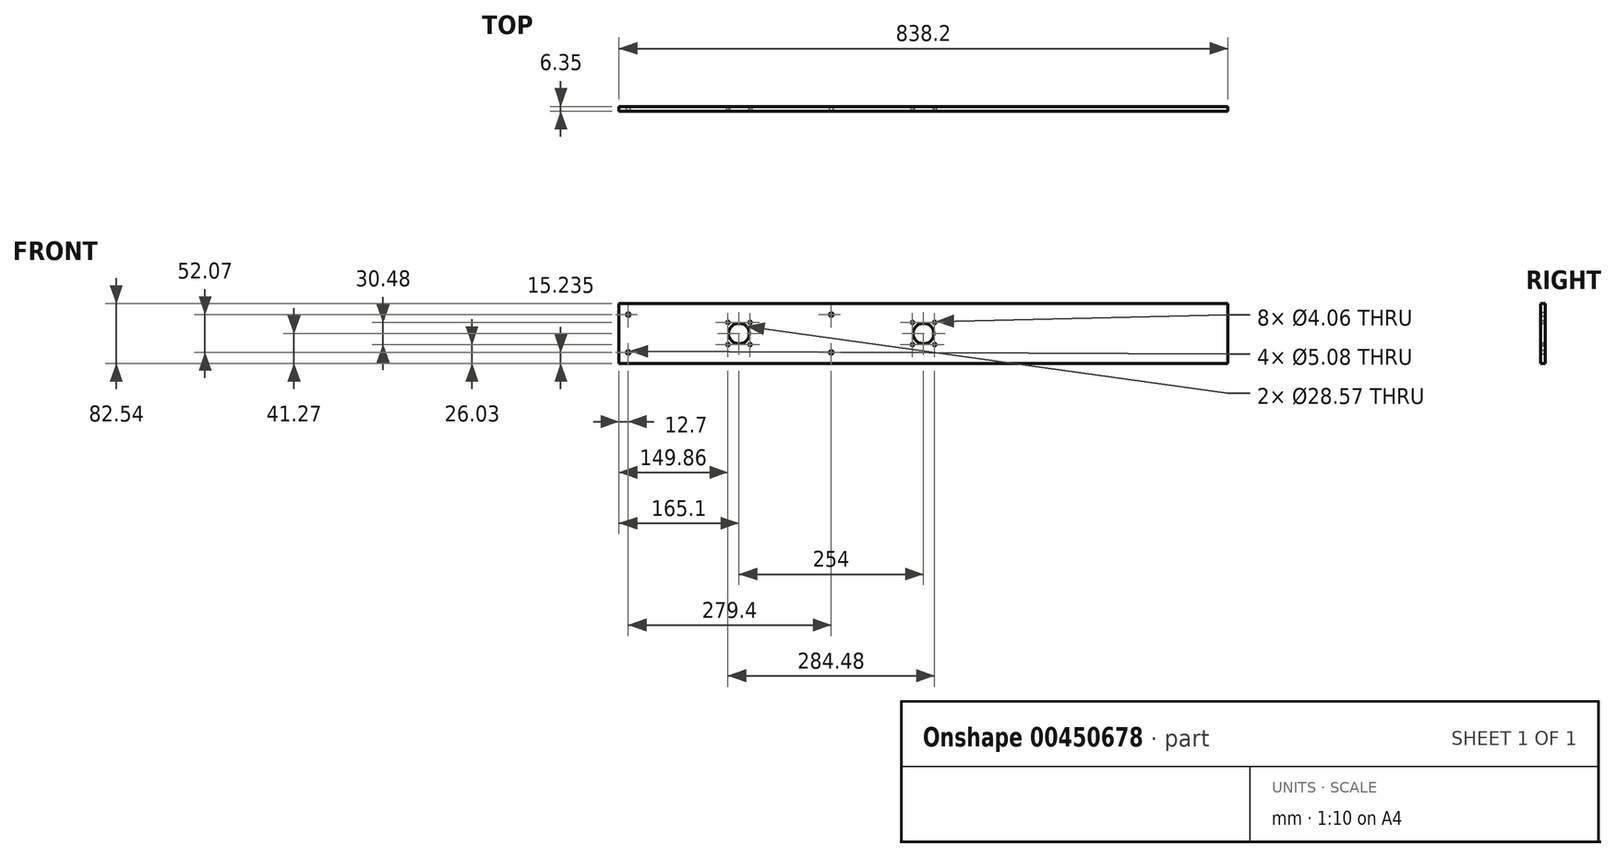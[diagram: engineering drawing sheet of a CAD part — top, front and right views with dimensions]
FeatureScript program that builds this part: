
annotation { "Feature Type Name" : "Feature", "Feature Type Description" : "" }
export const myFeature = defineFeature(function(context is Context, id is Id, definition is map)
    precondition{}
    {
        {
            var Q0;
            Q0=qCreatedBy(makeId("Front.planeOp"),FACE);
            var sketch = newSketch(context, id + "F0", { "sketchPlane" : qUnion([Q0])});
            skLineSegment(sketch, "E0.bottom", {"start": v(419.1, 41.28) * mm, "end": v(-419.1, 41.28) * mm});
            skLineSegment(sketch, "E0.top", {"start": v(419.1, -41.28) * mm, "end": v(-419.1, -41.28) * mm});
            skLineSegment(sketch, "E0.left", {"start": v(419.1, 41.28) * mm, "end": v(419.1, -41.28) * mm});
            skLineSegment(sketch, "E0.right", {"start": v(-419.1, 41.28) * mm, "end": v(-419.1, -41.28) * mm});
            skPoint(sketch, "E0.middle", {"position": v(0, 0) * mm});
            skSolve(sketch);
        }
        {
            var Q0;
            Q0=makeQuery(id+"F0.imprint","IMPRINT",FACE,{"disambiguationData":[TD([[makeQuery(id+"F0.imprint","IMPRINT",EDGE,{"derivedFrom":sQuery(id+"F0.wireOp",EDGE,"E0.bottom")}),1.0]])]});
            extrude(context, id + "F1", {"entities" : qUnion([Q0]), "depth" : 6.35 * mm});
        }
        {
            var Q0;
            Q0=makeQuery(id+"F1.opExtrude","CAP_FACE",FACE,{"disambiguationData":[OSD([sQuery(id+"F0.wireOp",EDGE,"E0.bottom"),sQuery(id+"F0.wireOp",EDGE,"E0.top"),sQuery(id+"F0.wireOp",EDGE,"E0.left"),sQuery(id+"F0.wireOp",EDGE,"E0.right")])],"isStart":false});
            var sketch = newSketch(context, id + "F2", { "sketchPlane" : qUnion([Q0])});
            skLineSegment(sketch, "E1", {"start": v(-419.1, 0) * mm, "end": v(-254, 0) * mm});
            skLineSegment(sketch, "E2", {"start": v(-254, 0) * mm, "end": v(-254, 15.24) * mm});
            skLineSegment(sketch, "E3", {"start": v(-254, 15.24) * mm, "end": v(-269.24, 15.24) * mm});
            skLineSegment(sketch, "E4", {"start": v(-269.24, 15.24) * mm, "end": v(-269.24, -15.24) * mm});
            skLineSegment(sketch, "E5", {"start": v(-269.24, -15.24) * mm, "end": v(-238.76, -15.24) * mm});
            skLineSegment(sketch, "E6", {"start": v(-238.76, -15.24) * mm, "end": v(-238.76, 15.24) * mm});
            skCircle(sketch, "E7", {"center": v(-269.24, 15.24) * mm, "radius": 2.03 * mm});
            skCircle(sketch, "E8", {"center": v(-269.24, -15.24) * mm, "radius": 2.03 * mm});
            skCircle(sketch, "E9", {"center": v(-238.76, -15.24) * mm, "radius": 2.03 * mm});
            skCircle(sketch, "E10", {"center": v(-238.76, 15.24) * mm, "radius": 2.03 * mm});
            skCircle(sketch, "E11", {"center": v(-254, 0) * mm, "radius": 14.29 * mm});
            skLineSegment(sketch, "E12", {"start": v(0, 0) * mm, "end": v(0, 15.24) * mm});
            skLineSegment(sketch, "E13", {"start": v(0, 15.24) * mm, "end": v(-15.24, 15.24) * mm});
            skLineSegment(sketch, "E14", {"start": v(-15.24, 15.24) * mm, "end": v(-15.24, -15.24) * mm});
            skLineSegment(sketch, "E15", {"start": v(-15.24, -15.24) * mm, "end": v(15.24, -15.24) * mm});
            skLineSegment(sketch, "E16", {"start": v(15.24, -15.24) * mm, "end": v(15.24, 15.24) * mm});
            skCircle(sketch, "E17", {"center": v(-15.24, 15.24) * mm, "radius": 2.03 * mm});
            skCircle(sketch, "E18", {"center": v(-15.24, -15.24) * mm, "radius": 2.03 * mm});
            skCircle(sketch, "E19", {"center": v(15.24, -15.24) * mm, "radius": 2.03 * mm});
            skCircle(sketch, "E20", {"center": v(15.24, 15.24) * mm, "radius": 2.03 * mm});
            skCircle(sketch, "E21", {"center": v(0, 0) * mm, "radius": 14.29 * mm});
            skSolve(sketch);
        }
        {
            var Q0;
            {var subQ0=sQuery(id+"F2.wireOp",EDGE,"E4");var subQ1=sQuery(id+"F2.wireOp",EDGE,"E3");var subQ2=makeQuery(id+"F2.imprint","INTERSECT",VERTEX,{"derivedFrom":[subQ1,subQ0]});Q0=makeQuery(id+"F2.imprint","IMPRINT",FACE,{"disambiguationData":[TD([[makeQuery(id+"F2.imprint","IMPRINT",EDGE,{"disambiguationData":[TD([[subQ2,1.0]])],"derivedFrom":subQ1}),-1.0]])]});}
            var Q1;
            {var subQ0=sQuery(id+"F2.wireOp",EDGE,"E4");var subQ1=sQuery(id+"F2.wireOp",EDGE,"E3");var subQ2=makeQuery(id+"F2.imprint","INTERSECT",VERTEX,{"derivedFrom":[subQ1,subQ0]});Q1=makeQuery(id+"F2.imprint","IMPRINT",FACE,{"disambiguationData":[TD([[makeQuery(id+"F2.imprint","IMPRINT",EDGE,{"disambiguationData":[TD([[subQ2,1.0]])],"derivedFrom":subQ1}),1.0]])]});}
            var Q2;
            {var subQ0=sQuery(id+"F2.wireOp",EDGE,"E2");var subQ1=sQuery(id+"F2.wireOp",EDGE,"E1");var subQ2=makeQuery(id+"F2.imprint","INTERSECT",VERTEX,{"derivedFrom":[subQ1,subQ0]});Q2=makeQuery(id+"F2.imprint","IMPRINT",FACE,{"disambiguationData":[TD([[makeQuery(id+"F2.imprint","IMPRINT",EDGE,{"disambiguationData":[TD([[subQ2,1.0]])],"derivedFrom":subQ1}),-1.0]])]});}
            var Q3;
            {var subQ0=sQuery(id+"F2.wireOp",EDGE,"E2");var subQ1=sQuery(id+"F2.wireOp",EDGE,"E1");var subQ2=makeQuery(id+"F2.imprint","INTERSECT",VERTEX,{"derivedFrom":[subQ1,subQ0]});Q3=makeQuery(id+"F2.imprint","IMPRINT",FACE,{"disambiguationData":[TD([[makeQuery(id+"F2.imprint","IMPRINT",EDGE,{"disambiguationData":[TD([[subQ2,1.0]])],"derivedFrom":subQ1}),1.0]])]});}
            var Q4;
            {var subQ0=sQuery(id+"F2.wireOp",EDGE,"E5");var subQ1=sQuery(id+"F2.wireOp",EDGE,"E4");var subQ2=makeQuery(id+"F2.imprint","INTERSECT",VERTEX,{"derivedFrom":[subQ1,subQ0]});Q4=makeQuery(id+"F2.imprint","IMPRINT",FACE,{"disambiguationData":[TD([[makeQuery(id+"F2.imprint","IMPRINT",EDGE,{"disambiguationData":[TD([[subQ2,1.0]])],"derivedFrom":subQ1}),-1.0]])]});}
            var Q5;
            {var subQ0=sQuery(id+"F2.wireOp",EDGE,"E5");var subQ1=sQuery(id+"F2.wireOp",EDGE,"E4");var subQ2=makeQuery(id+"F2.imprint","INTERSECT",VERTEX,{"derivedFrom":[subQ1,subQ0]});Q5=makeQuery(id+"F2.imprint","IMPRINT",FACE,{"disambiguationData":[TD([[makeQuery(id+"F2.imprint","IMPRINT",EDGE,{"disambiguationData":[TD([[subQ2,1.0]])],"derivedFrom":subQ1}),1.0]])]});}
            var Q6;
            {var subQ0=sQuery(id+"F2.wireOp",EDGE,"E6");var subQ1=sQuery(id+"F2.wireOp",EDGE,"E5");var subQ2=makeQuery(id+"F2.imprint","INTERSECT",VERTEX,{"derivedFrom":[subQ1,subQ0]});Q6=makeQuery(id+"F2.imprint","IMPRINT",FACE,{"disambiguationData":[TD([[makeQuery(id+"F2.imprint","IMPRINT",EDGE,{"disambiguationData":[TD([[subQ2,1.0]])],"derivedFrom":subQ1}),-1.0]])]});}
            var Q7;
            {var subQ0=sQuery(id+"F2.wireOp",EDGE,"E6");var subQ1=sQuery(id+"F2.wireOp",EDGE,"E5");var subQ2=makeQuery(id+"F2.imprint","INTERSECT",VERTEX,{"derivedFrom":[subQ1,subQ0]});Q7=makeQuery(id+"F2.imprint","IMPRINT",FACE,{"disambiguationData":[TD([[makeQuery(id+"F2.imprint","IMPRINT",EDGE,{"disambiguationData":[TD([[subQ2,1.0]])],"derivedFrom":subQ1}),1.0]])]});}
            var Q8;
            Q8=makeQuery(id+"F2.imprint","IMPRINT",FACE,{"disambiguationData":[TD([[makeQuery(id+"F2.imprint","IMPRINT",EDGE,{"derivedFrom":sQuery(id+"F2.wireOp",EDGE,"E10")}),1.0]])]});
            var Q9;
            Q9=makeQuery(id+"F2.imprint","IMPRINT",FACE,{"disambiguationData":[TD([[makeQuery(id+"F2.imprint","IMPRINT",EDGE,{"derivedFrom":sQuery(id+"F2.wireOp",EDGE,"E21")}),1.0]])]});
            var Q10;
            {var subQ0=sQuery(id+"F2.wireOp",EDGE,"E16");var subQ1=sQuery(id+"F2.wireOp",EDGE,"E15");var subQ2=makeQuery(id+"F2.imprint","INTERSECT",VERTEX,{"derivedFrom":[subQ1,subQ0]});Q10=makeQuery(id+"F2.imprint","IMPRINT",FACE,{"disambiguationData":[TD([[makeQuery(id+"F2.imprint","IMPRINT",EDGE,{"disambiguationData":[TD([[subQ2,1.0]])],"derivedFrom":subQ1}),-1.0]])]});}
            var Q11;
            {var subQ0=sQuery(id+"F2.wireOp",EDGE,"E16");var subQ1=sQuery(id+"F2.wireOp",EDGE,"E15");var subQ2=makeQuery(id+"F2.imprint","INTERSECT",VERTEX,{"derivedFrom":[subQ1,subQ0]});Q11=makeQuery(id+"F2.imprint","IMPRINT",FACE,{"disambiguationData":[TD([[makeQuery(id+"F2.imprint","IMPRINT",EDGE,{"disambiguationData":[TD([[subQ2,1.0]])],"derivedFrom":subQ1}),1.0]])]});}
            var Q12;
            Q12=makeQuery(id+"F2.imprint","IMPRINT",FACE,{"disambiguationData":[TD([[makeQuery(id+"F2.imprint","IMPRINT",EDGE,{"derivedFrom":sQuery(id+"F2.wireOp",EDGE,"E20")}),1.0]])]});
            var Q13;
            {var subQ0=sQuery(id+"F2.wireOp",EDGE,"E14");var subQ1=sQuery(id+"F2.wireOp",EDGE,"E13");var subQ2=makeQuery(id+"F2.imprint","INTERSECT",VERTEX,{"derivedFrom":[subQ1,subQ0]});Q13=makeQuery(id+"F2.imprint","IMPRINT",FACE,{"disambiguationData":[TD([[makeQuery(id+"F2.imprint","IMPRINT",EDGE,{"disambiguationData":[TD([[subQ2,1.0]])],"derivedFrom":subQ1}),-1.0]])]});}
            var Q14;
            {var subQ0=sQuery(id+"F2.wireOp",EDGE,"E14");var subQ1=sQuery(id+"F2.wireOp",EDGE,"E13");var subQ2=makeQuery(id+"F2.imprint","INTERSECT",VERTEX,{"derivedFrom":[subQ1,subQ0]});Q14=makeQuery(id+"F2.imprint","IMPRINT",FACE,{"disambiguationData":[TD([[makeQuery(id+"F2.imprint","IMPRINT",EDGE,{"disambiguationData":[TD([[subQ2,1.0]])],"derivedFrom":subQ1}),1.0]])]});}
            var Q15;
            {var subQ0=sQuery(id+"F2.wireOp",EDGE,"E15");var subQ1=sQuery(id+"F2.wireOp",EDGE,"E14");var subQ2=makeQuery(id+"F2.imprint","INTERSECT",VERTEX,{"derivedFrom":[subQ1,subQ0]});Q15=makeQuery(id+"F2.imprint","IMPRINT",FACE,{"disambiguationData":[TD([[makeQuery(id+"F2.imprint","IMPRINT",EDGE,{"disambiguationData":[TD([[subQ2,1.0]])],"derivedFrom":subQ1}),-1.0]])]});}
            var Q16;
            {var subQ0=sQuery(id+"F2.wireOp",EDGE,"E15");var subQ1=sQuery(id+"F2.wireOp",EDGE,"E14");var subQ2=makeQuery(id+"F2.imprint","INTERSECT",VERTEX,{"derivedFrom":[subQ1,subQ0]});Q16=makeQuery(id+"F2.imprint","IMPRINT",FACE,{"disambiguationData":[TD([[makeQuery(id+"F2.imprint","IMPRINT",EDGE,{"disambiguationData":[TD([[subQ2,1.0]])],"derivedFrom":subQ1}),1.0]])]});}
            var Q17;
            Q17=makeQuery(id+"F1.opExtrude","CAP_FACE",FACE,{"disambiguationData":[OSD([sQuery(id+"F0.wireOp",EDGE,"E0.bottom"),sQuery(id+"F0.wireOp",EDGE,"E0.top"),sQuery(id+"F0.wireOp",EDGE,"E0.left"),sQuery(id+"F0.wireOp",EDGE,"E0.right")])],"isStart":true});
            extrude(context, id + "F3", {"entities" : qUnion([Q0, Q1, Q2, Q3, Q4, Q5, Q6, Q7, Q8, Q9, Q10, Q11, Q12, Q13, Q14, Q15, Q16]), "operationType" : NewBodyOperationType.REMOVE, "endBound" : BoundingType.UP_TO_SURFACE, "oppositeDirection" : true, "endBoundEntityFace" : qUnion([Q17]), "depth" : 25.4 * mm});
        }
        {
            var Q0;
            Q0=makeQuery(id+"F1.opExtrude","CAP_FACE",FACE,{"disambiguationData":[OSD([sQuery(id+"F0.wireOp",EDGE,"E0.bottom"),sQuery(id+"F0.wireOp",EDGE,"E0.top"),sQuery(id+"F0.wireOp",EDGE,"E0.left"),sQuery(id+"F0.wireOp",EDGE,"E0.right")])],"isStart":false});
            var sketch = newSketch(context, id + "F4", { "sketchPlane" : qUnion([Q0])});
            skLineSegment(sketch, "E22", {"start": v(-406.4, 41.28) * mm, "end": v(-406.4, -41.28) * mm});
            skPoint(sketch, "E23", {"position": v(-406.4, 26.04) * mm});
            skPoint(sketch, "E24", {"position": v(-406.4, -26.04) * mm});
            skCircle(sketch, "E25", {"center": v(-406.4, 26.04) * mm, "radius": 2.54 * mm});
            skCircle(sketch, "E26", {"center": v(-406.4, -26.04) * mm, "radius": 2.54 * mm});
            skLineSegment(sketch, "E27", {"start": v(-254, 0) * mm, "end": v(-254, 41.28) * mm});
            skLineSegment(sketch, "E28", {"start": v(-254, 41.28) * mm, "end": v(0, 41.28) * mm});
            skLineSegment(sketch, "E29", {"start": v(-127, 41.28) * mm, "end": v(-127, -41.28) * mm});
            skPoint(sketch, "E30", {"position": v(-127, -26.04) * mm});
            skPoint(sketch, "E31", {"position": v(-127, 26.04) * mm});
            skCircle(sketch, "E32", {"center": v(-127, -26.04) * mm, "radius": 2.54 * mm});
            skCircle(sketch, "E33", {"center": v(-127, 26.04) * mm, "radius": 2.54 * mm});
            skSolve(sketch);
        }
        {
            var Q0;
            Q0=qSketchRegion(id+"F4",true);
            var Q1;
            Q1=makeQuery(id+"F1.opExtrude","CAP_FACE",FACE,{"disambiguationData":[OSD([sQuery(id+"F0.wireOp",EDGE,"E0.bottom"),sQuery(id+"F0.wireOp",EDGE,"E0.top"),sQuery(id+"F0.wireOp",EDGE,"E0.left"),sQuery(id+"F0.wireOp",EDGE,"E0.right")])],"isStart":true});
            extrude(context, id + "F5", {"entities" : qUnion([Q0]), "operationType" : NewBodyOperationType.REMOVE, "endBound" : BoundingType.UP_TO_SURFACE, "oppositeDirection" : true, "endBoundEntityFace" : qUnion([Q1]), "depth" : 25.4 * mm});
        }
    });
